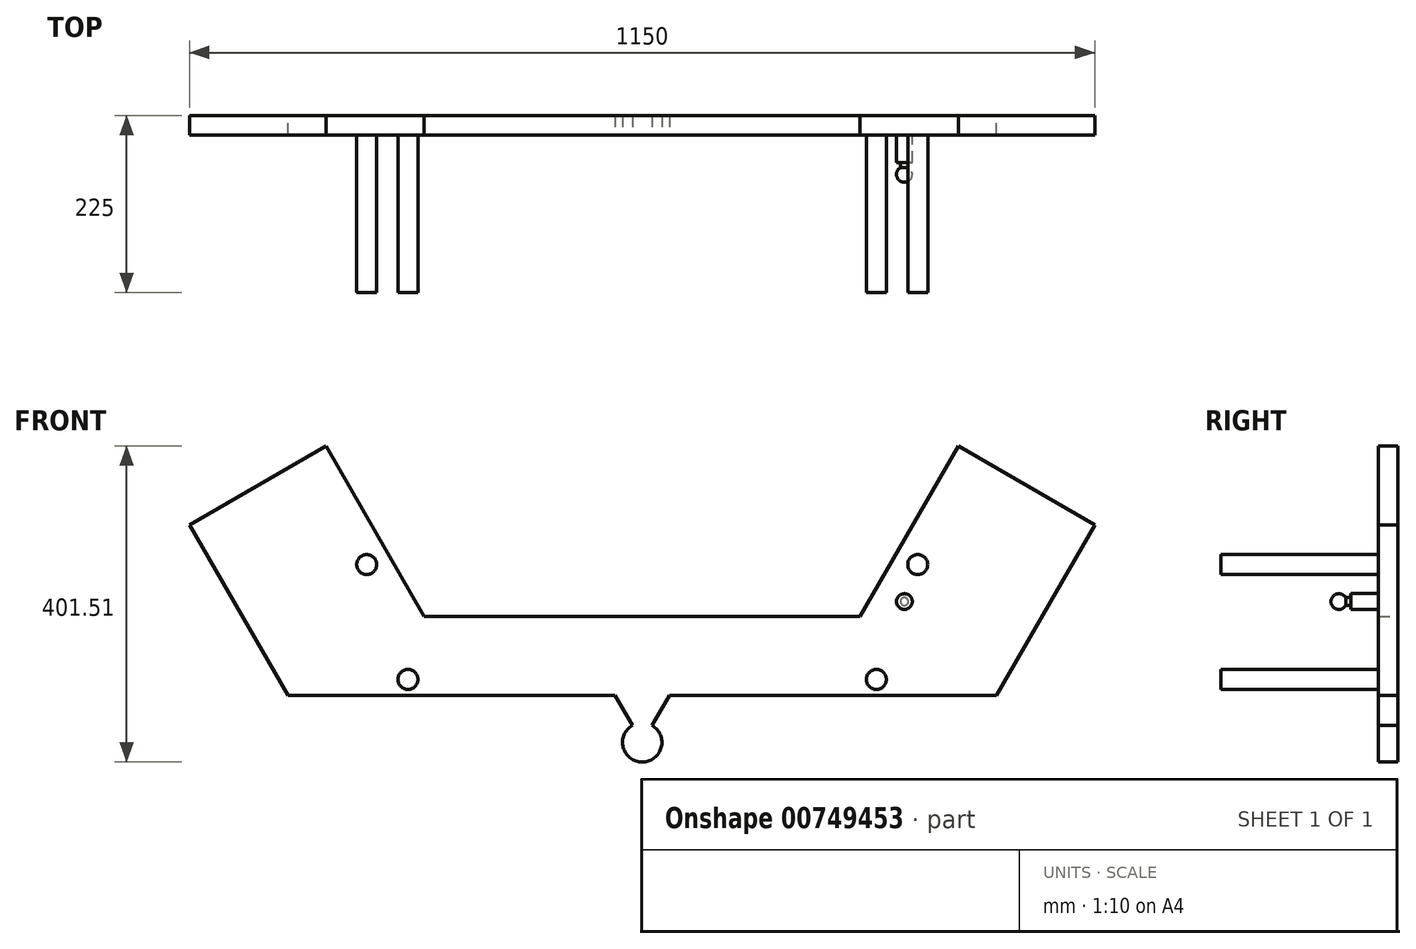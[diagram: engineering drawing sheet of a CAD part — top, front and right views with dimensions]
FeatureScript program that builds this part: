
annotation { "Feature Type Name" : "Feature", "Feature Type Description" : "" }
export const myFeature = defineFeature(function(context is Context, id is Id, definition is map)
    precondition{}
    {
        {
            var Q0;
            Q0=qCreatedBy(makeId("Front.planeOp"),FACE);
            var sketch = newSketch(context, id + "F0", { "sketchPlane" : qUnion([Q0])});
            skLineSegment(sketch, "E0", {"start": v(0, 100) * mm, "end": v(450, 100) * mm});
            skLineSegment(sketch, "E1", {"start": v(450, 100) * mm, "end": v(575, 316.5) * mm});
            skLineSegment(sketch, "E2", {"start": v(575, 316.5) * mm, "end": v(401.8, 416.5) * mm});
            skLineSegment(sketch, "E3", {"start": v(401.8, 416.5) * mm, "end": v(276.8, 200) * mm});
            skLineSegment(sketch, "E4", {"start": v(276.8, 200) * mm, "end": v(0, 200) * mm});
            skLineSegment(sketch, "E5", {"start": v(0, 200) * mm, "end": v(0, 100) * mm});
            skSolve(sketch);
        }
        {
            var Q0;
            Q0=makeQuery(id+"F0.imprint","IMPRINT",FACE,{"disambiguationData":[TD([[makeQuery(id+"F0.imprint","IMPRINT",EDGE,{"derivedFrom":sQuery(id+"F0.wireOp",EDGE,"E0")}),1.0]])]});
            extrude(context, id + "F1", {"entities" : qUnion([Q0]), "depth" : 25 * mm, "offsetDistance" : 25 * mm});
        }
        {
            var Q0;
            Q0=makeQuery(id+"F1.opExtrude","CAP_FACE",FACE,{"disambiguationData":[OSD([sQuery(id+"F0.wireOp",EDGE,"E0"),sQuery(id+"F0.wireOp",EDGE,"E1"),sQuery(id+"F0.wireOp",EDGE,"E2"),sQuery(id+"F0.wireOp",EDGE,"E3"),sQuery(id+"F0.wireOp",EDGE,"E4"),sQuery(id+"F0.wireOp",EDGE,"E5")])],"isStart":false});
            var sketch = newSketch(context, id + "F2", { "sketchPlane" : qUnion([Q0])});
            skCircle(sketch, "E6", {"center": v(350, 266) * mm, "radius": 12.7 * mm});
            skCircle(sketch, "E7", {"center": v(297.5, 120) * mm, "radius": 12.7 * mm});
            skCircle(sketch, "E8", {"center": v(297.5, 96) * mm, "radius": 2.5 * mm});
            skLineSegment(sketch, "E9", {"start": v(350, 266) * mm, "end": v(297.5, 120) * mm});
            skSolve(sketch);
        }
        {
            var Q0;
            Q0=makeQuery(id+"F2.imprint","IMPRINT",FACE,{"disambiguationData":[TD([[makeQuery(id+"F2.imprint","IMPRINT",EDGE,{"derivedFrom":sQuery(id+"F2.wireOp",EDGE,"E6")}),1.0]])]});
            var Q1;
            Q1=makeQuery(id+"F2.imprint","IMPRINT",FACE,{"disambiguationData":[TD([[makeQuery(id+"F2.imprint","IMPRINT",EDGE,{"derivedFrom":sQuery(id+"F2.wireOp",EDGE,"E7")}),1.0]])]});
            extrude(context, id + "F3", {"entities" : qUnion([Q0, Q1]), "operationType" : NewBodyOperationType.ADD, "depth" : 200 * mm, "offsetDistance" : 25 * mm});
        }
        {
            var Q0;
            Q0=makeQuery(id+"F1.opExtrude","SWEPT_BODY",BODY,{"disambiguationData":[OSD([sQuery(id+"F0.wireOp",EDGE,"E0"),sQuery(id+"F0.wireOp",EDGE,"E1"),sQuery(id+"F0.wireOp",EDGE,"E2"),sQuery(id+"F0.wireOp",EDGE,"E3"),sQuery(id+"F0.wireOp",EDGE,"E4"),sQuery(id+"F0.wireOp",EDGE,"E5")])]});
            var Q1;
            Q1=qCreatedBy(makeId("Right.planeOp"),FACE);
            mirror(context, id + "F4", {"operationType" : NewBodyOperationType.ADD, "entities" : qUnion([Q0]), "mirrorPlane" : qUnion([Q1])});
        }
        {
            var Q0;
            {var subQ0=makeQuery(id+"F1.opExtrude","CAP_FACE",FACE,{"disambiguationData":[OSD([sQuery(id+"F0.wireOp",EDGE,"E0"),sQuery(id+"F0.wireOp",EDGE,"E1"),sQuery(id+"F0.wireOp",EDGE,"E2"),sQuery(id+"F0.wireOp",EDGE,"E3"),sQuery(id+"F0.wireOp",EDGE,"E4"),sQuery(id+"F0.wireOp",EDGE,"E5")])],"isStart":false});Q0=makeQuery(id+"F4.boolean.opBoolean","MERGE",FACE,{"derivedFrom":[subQ0,makeQuery(id+"F4.opPattern","COPY",FACE,{"derivedFrom":subQ0,"instanceName":"1"})]});}
            var sketch = newSketch(context, id + "F5", { "sketchPlane" : qUnion([Q0])});
            skArc(sketch, "E10", {"start": v(-12.5, 61.65) * mm, "mid": v(0, 15) * mm, "end": v(12.5, 61.65) * mm});
            skLineSegment(sketch, "E11", {"start": v(-12.5, 61.65) * mm, "end": v(-34.64, 100) * mm});
            skLineSegment(sketch, "E12", {"start": v(34.64, 100) * mm, "end": v(12.5, 61.65) * mm});
            skSolve(sketch);
        }
        {
            var Q0;
            Q0 = qSketchRegion(id + "F5", true);
            var Q1;
            Q1=makeQuery(id+"F5.imprint","IMPRINT",FACE,{"disambiguationData":[TD([[makeQuery(id+"F5.imprint","IMPRINT",EDGE,{"derivedFrom":sQuery(id+"F5.wireOp",EDGE,"E10")}),1.0]])]});
            extrude(context, id + "F6", {"entities" : qUnion([Q0, Q1]), "operationType" : NewBodyOperationType.ADD, "oppositeDirection" : true, "depth" : 25 * mm, "offsetDistance" : 25 * mm});
        }
        {
            var Q0;
            Q0=sQuery(id+"F2.wireOp",EDGE,"E9");
            cPlane(context, id + "F7", {"entities" : qUnion([Q0]), "cplaneType" : CPlaneType.LINE_ANGLE, "offset" : 25 * mm, "angle" : 0 * degree, "oppositeDirection" : true, "width" : 150 * mm, "height" : 150 * mm});
        }
        {
            var Q0;
            Q0=qCreatedBy(id+"F7.planeOp",FACE);
            var sketch = newSketch(context, id + "F8", { "sketchPlane" : qUnion([Q0])});
            skLineSegment(sketch, "E13.0.0", {"start": v(25, 527.9) * mm, "end": v(25, 281.86) * mm, "construction": true});
            skLineSegment(sketch, "E13.0.1", {"start": v(25, 281.86) * mm, "end": v(25, 188.2) * mm, "construction": true});
            skLineSegment(sketch, "E13.0.2", {"start": v(25, 188.2) * mm, "end": v(25, 94.1) * mm, "construction": true});
            skLineSegment(sketch, "E13.0.3", {"start": v(25, 94.1) * mm, "end": v(25, 246.37) * mm});
            skLineSegment(sketch, "E13.0.4", {"start": v(25, 246.37) * mm, "end": v(25, 492.4) * mm});
            skLineSegment(sketch, "E13.0.5", {"start": v(25, 492.4) * mm, "end": v(25, 527.9) * mm});
            skLineSegment(sketch, "E14", {"start": v(25, 318.74) * mm, "end": v(85, 318.74) * mm});
            skLineSegment(sketch, "E15", {"start": v(25, 328.74) * mm, "end": v(60, 328.74) * mm});
            skLineSegment(sketch, "E16", {"start": v(60, 328.74) * mm, "end": v(60, 323.74) * mm});
            skLineSegment(sketch, "E17", {"start": v(60, 323.74) * mm, "end": v(66.34, 323.74) * mm});
            skArc(sketch, "E18", {"start": v(66.34, 323.74) * mm, "mid": v(77.59, 328.4) * mm, "end": v(85, 318.74) * mm});
            skLineSegment(sketch, "E19", {"start": v(25, 328.74) * mm, "end": v(25, 318.74) * mm});
            skSolve(sketch);
        }
        {
            var Q0;
            Q0=makeQuery(id+"F8.imprint","IMPRINT",FACE,{"disambiguationData":[TD([[makeQuery(id+"F8.imprint","IMPRINT",EDGE,{"derivedFrom":sQuery(id+"F8.wireOp",EDGE,"E14")}),1.0]])]});
            var Q1;
            Q1=sQuery(id+"F8.wireOp",EDGE,"E14");
            revolve(context, id + "F9", {"operationType" : NewBodyOperationType.ADD, "surfaceOperationType" : NewSurfaceOperationType.NEW, "entities" : qUnion([Q0]), "axis" : qUnion([Q1]), "revolveType" : RevolveType.FULL});
        }
    });
